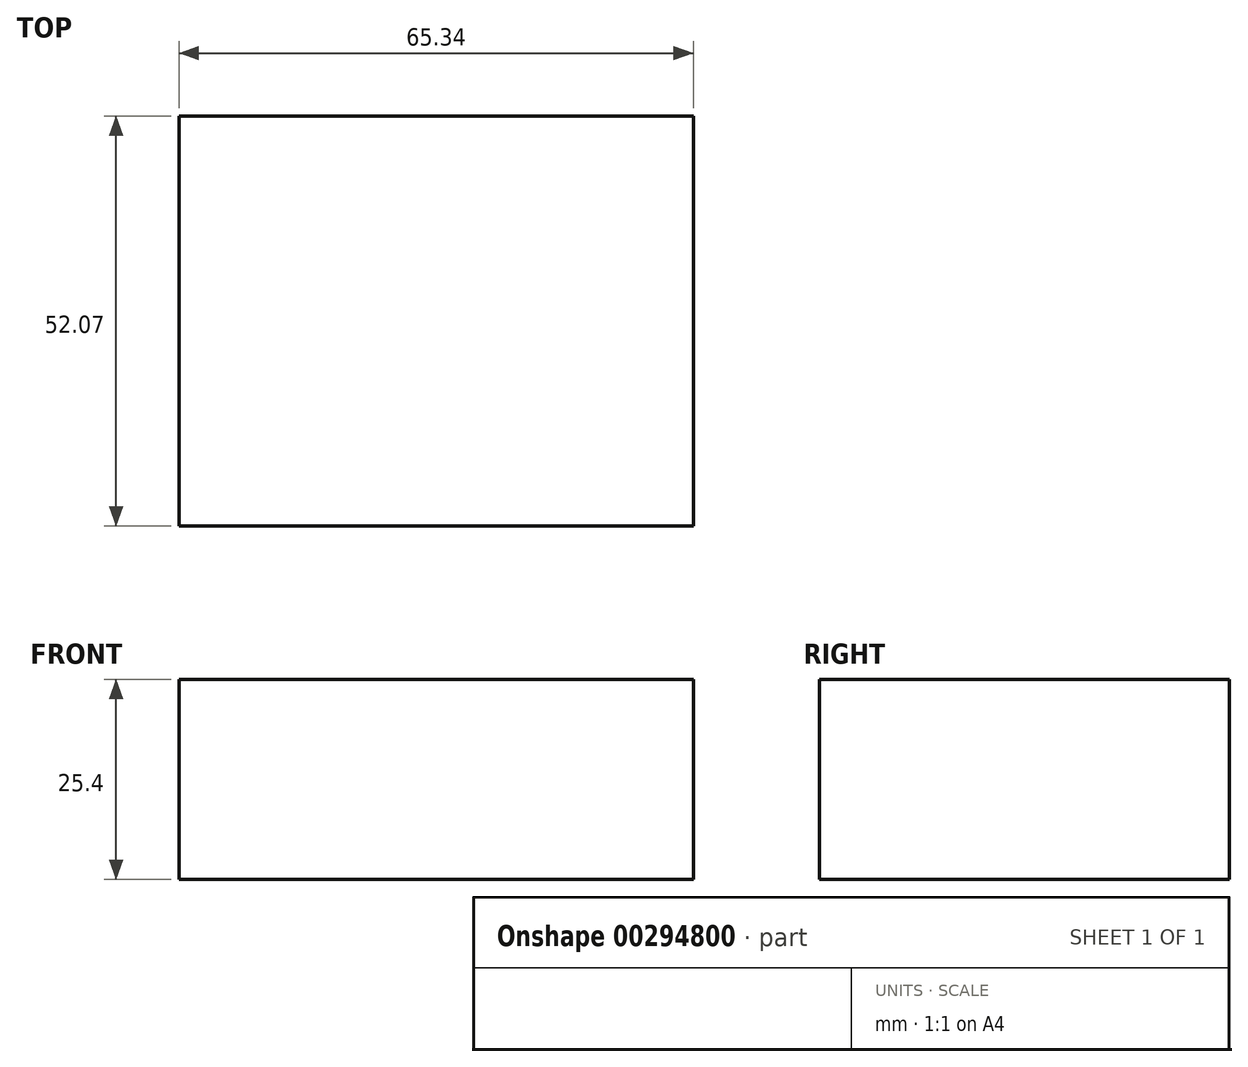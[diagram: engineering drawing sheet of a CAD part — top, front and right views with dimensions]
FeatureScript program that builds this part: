
annotation { "Feature Type Name" : "Feature", "Feature Type Description" : "" }
export const myFeature = defineFeature(function(context is Context, id is Id, definition is map)
    precondition{}
    {
        {
            var Q0;
            Q0=qCreatedBy(makeId("Top.planeOp"),FACE);
            var sketch = newSketch(context, id + "F0", { "sketchPlane" : qUnion([Q0])});
            skLineSegment(sketch, "E0.bottom", {"start": v(0, 52.07) * mm, "end": v(65.34, 52.07) * mm});
            skLineSegment(sketch, "E0.top", {"start": v(0, 0) * mm, "end": v(65.34, 0) * mm});
            skLineSegment(sketch, "E0.left", {"start": v(0, 52.07) * mm, "end": v(0, 0) * mm});
            skLineSegment(sketch, "E0.right", {"start": v(65.34, 52.07) * mm, "end": v(65.34, 0) * mm});
            skSolve(sketch);
        }
        {
            var Q0;
            Q0=makeQuery(id+"F0.imprint","IMPRINT",FACE,{"disambiguationData":[TD([[makeQuery(id+"F0.imprint","IMPRINT",EDGE,{"derivedFrom":sQuery(id+"F0.wireOp",EDGE,"E0.bottom")}),-1.0]])]});
            extrude(context, id + "F1", {"entities" : qUnion([Q0]), "depth" : 25.4 * mm});
        }
    });
